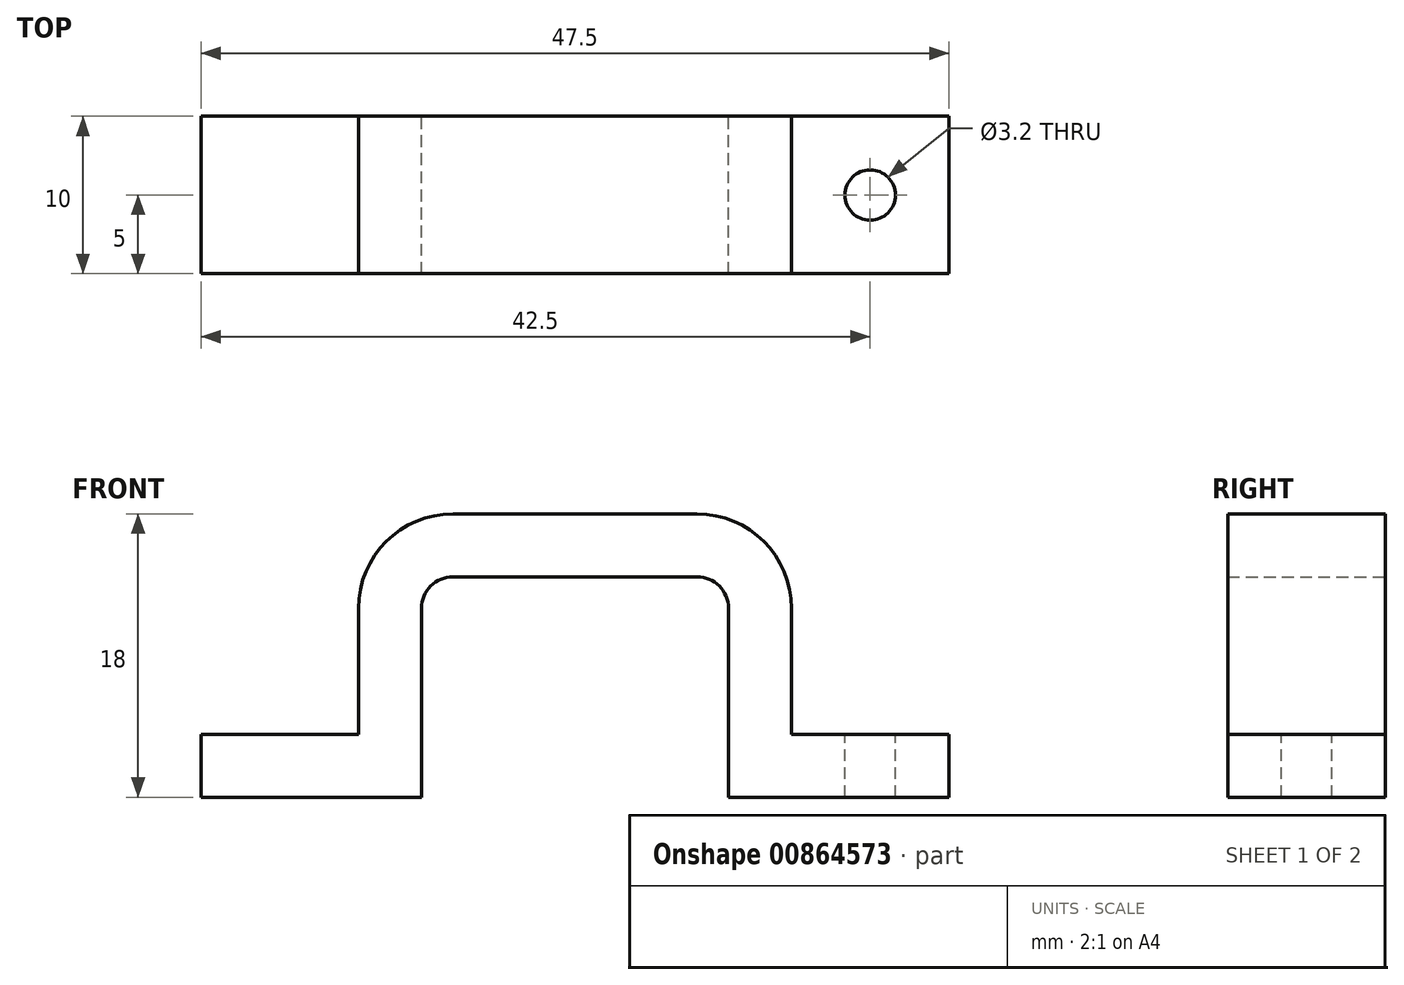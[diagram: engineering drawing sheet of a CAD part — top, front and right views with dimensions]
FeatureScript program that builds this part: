
annotation { "Feature Type Name" : "Feature", "Feature Type Description" : "" }
export const myFeature = defineFeature(function(context is Context, id is Id, definition is map)
    precondition{}
    {
        {
            var Q0;
            Q0=qCreatedBy(makeId("Front.planeOp"),FACE);
            var sketch = newSketch(context, id + "F0", { "sketchPlane" : qUnion([Q0])});
            skLineSegment(sketch, "E0.bottom", {"start": v(7.75, 7) * mm, "end": v(-7.75, 7) * mm});
            skLineSegment(sketch, "E0.top", {"start": v(9.75, -7) * mm, "end": v(-9.75, -7) * mm});
            skLineSegment(sketch, "E0.left", {"start": v(9.75, 5) * mm, "end": v(9.75, -7) * mm});
            skLineSegment(sketch, "E0.right", {"start": v(-9.75, 5) * mm, "end": v(-9.75, -7) * mm});
            skPoint(sketch, "E0.middle", {"position": v(0, 0) * mm});
            skPoint(sketch, "E1.visualSharp", {"position": v(-9.75, 7) * mm});
            skArc(sketch, "E1.filletArc", {"start": v(-7.75, 7) * mm, "mid": v(-9.16, 6.41) * mm, "end": v(-9.75, 5) * mm});
            skPoint(sketch, "E2.visualSharp", {"position": v(9.75, 7) * mm});
            skArc(sketch, "E2.filletArc", {"start": v(9.75, 5) * mm, "mid": v(9.16, 6.41) * mm, "end": v(7.75, 7) * mm});
            skLineSegment(sketch, "E3.0", {"start": v(13.75, 5) * mm, "end": v(13.75, -7) * mm});
            skLineSegment(sketch, "E3.1", {"start": v(-13.75, 5) * mm, "end": v(-13.75, -7) * mm});
            skArc(sketch, "E3.2", {"start": v(-7.75, 11) * mm, "mid": v(-12, 9.24) * mm, "end": v(-13.75, 5) * mm});
            skLineSegment(sketch, "E3.3", {"start": v(7.75, 11) * mm, "end": v(-7.75, 11) * mm});
            skArc(sketch, "E3.4", {"start": v(13.75, 5) * mm, "mid": v(12, 9.24) * mm, "end": v(7.75, 11) * mm});
            skLineSegment(sketch, "E4.bottom", {"start": v(9.75, -7) * mm, "end": v(23.75, -7) * mm});
            skLineSegment(sketch, "E4.top", {"start": v(9.75, -3) * mm, "end": v(23.75, -3) * mm});
            skLineSegment(sketch, "E4.left", {"start": v(9.75, -7) * mm, "end": v(9.75, -3) * mm});
            skLineSegment(sketch, "E4.right", {"start": v(23.75, -7) * mm, "end": v(23.75, -3) * mm});
            skLineSegment(sketch, "E5.MirrorCS", {"start": v(-9.75, -3) * mm, "end": v(-23.75, -3) * mm});
            skLineSegment(sketch, "E6.MirrorCS", {"start": v(-23.75, -7) * mm, "end": v(-23.75, -3) * mm});
            skLineSegment(sketch, "E7.MirrorCS", {"start": v(-9.75, -7) * mm, "end": v(-23.75, -7) * mm});
            skSolve(sketch);
        }
        {
            var Q0;
            Q0=makeQuery(id+"F0.imprint","IMPRINT",FACE,{"disambiguationData":[TD([[makeQuery(id+"F0.imprint","IMPRINT",EDGE,{"derivedFrom":sQuery(id+"F0.wireOp",EDGE,"E0.bottom")}),-1.0]])]});
            var Q1;
            {var subQ0=sQuery(id+"F0.wireOp",EDGE,"E4.bottom");var subQ5=sQuery(id+"F0.wireOp",EDGE,"E3.0");var subQ7=makeQuery(id+"F0.imprint","INTERSECT",VERTEX,{"derivedFrom":[subQ5,subQ0]});Q1=makeQuery(id+"F0.imprint","IMPRINT",FACE,{"disambiguationData":[TD([[makeQuery(id+"F0.imprint","IMPRINT",EDGE,{"disambiguationData":[TD([[subQ7,1.0]])],"derivedFrom":subQ5}),-1.0]])]});}
            var Q2;
            {var subQ5=sQuery(id+"F0.wireOp",EDGE,"E4.right");Q2=makeQuery(id+"F0.imprint","IMPRINT",FACE,{"disambiguationData":[TD([[makeQuery(id+"F0.imprint","IMPRINT",EDGE,{"derivedFrom":subQ5}),1.0]])]});}
            var Q3;
            {var subQ0=sQuery(id+"F0.wireOp",EDGE,"E7.MirrorCS");var subQ5=sQuery(id+"F0.wireOp",EDGE,"E3.1");var subQ6=makeQuery(id+"F0.imprint","INTERSECT",VERTEX,{"derivedFrom":[subQ5,subQ0]});Q3=makeQuery(id+"F0.imprint","IMPRINT",FACE,{"disambiguationData":[TD([[makeQuery(id+"F0.imprint","IMPRINT",EDGE,{"disambiguationData":[TD([[subQ6,1.0]])],"derivedFrom":subQ5}),1.0]])]});}
            var Q4;
            {var subQ5=sQuery(id+"F0.wireOp",EDGE,"E6.MirrorCS");Q4=makeQuery(id+"F0.imprint","IMPRINT",FACE,{"disambiguationData":[TD([[makeQuery(id+"F0.imprint","IMPRINT",EDGE,{"derivedFrom":subQ5}),-1.0]])]});}
            extrude(context, id + "F1", {"entities" : qUnion([Q0, Q1, Q2, Q3, Q4]), "depth" : 10 * mm, "offsetDistance" : 25 * mm});
        }
        {
            var Q0;
            Q0=makeQuery(id+"F1.opExtrude","SWEPT_FACE",FACE,{"disambiguationData":[OSD([sQuery(id+"F0.wireOp",EDGE,"E4.top")])]});
            var sketch = newSketch(context, id + "F2", { "sketchPlane" : qUnion([Q0])});
            skLineSegment(sketch, "E8", {"start": v(18.75, 0) * mm, "end": v(18.75, -10) * mm, "construction": true});
            skCircle(sketch, "E9", {"center": v(18.75, -5) * mm, "radius": 1.6 * mm});
            skCircle(sketch, "E10.MirrorC", {"center": v(-18.75, -5) * mm, "radius": 1.6 * mm});
            skSolve(sketch);
        }
        {
            var Q0;
            Q0=makeQuery(id+"F2.imprint","IMPRINT",FACE,{"disambiguationData":[TD([[makeQuery(id+"F2.imprint","IMPRINT",EDGE,{"derivedFrom":sQuery(id+"F2.wireOp",EDGE,"E9")}),1.0]])]});
            var Q1;
            Q1=makeQuery(id+"F2.imprint","IMPRINT",FACE,{"disambiguationData":[TD([[makeQuery(id+"F2.imprint","IMPRINT",EDGE,{"derivedFrom":sQuery(id+"F2.wireOp",EDGE,"E10.MirrorC")}),-1.0]])]});
            extrude(context, id + "F3", {"entities" : qUnion([Q0, Q1]), "operationType" : NewBodyOperationType.REMOVE, "endBound" : BoundingType.THROUGH_ALL, "oppositeDirection" : true, "depth" : 25 * mm, "offsetDistance" : 25 * mm});
        }
    });
